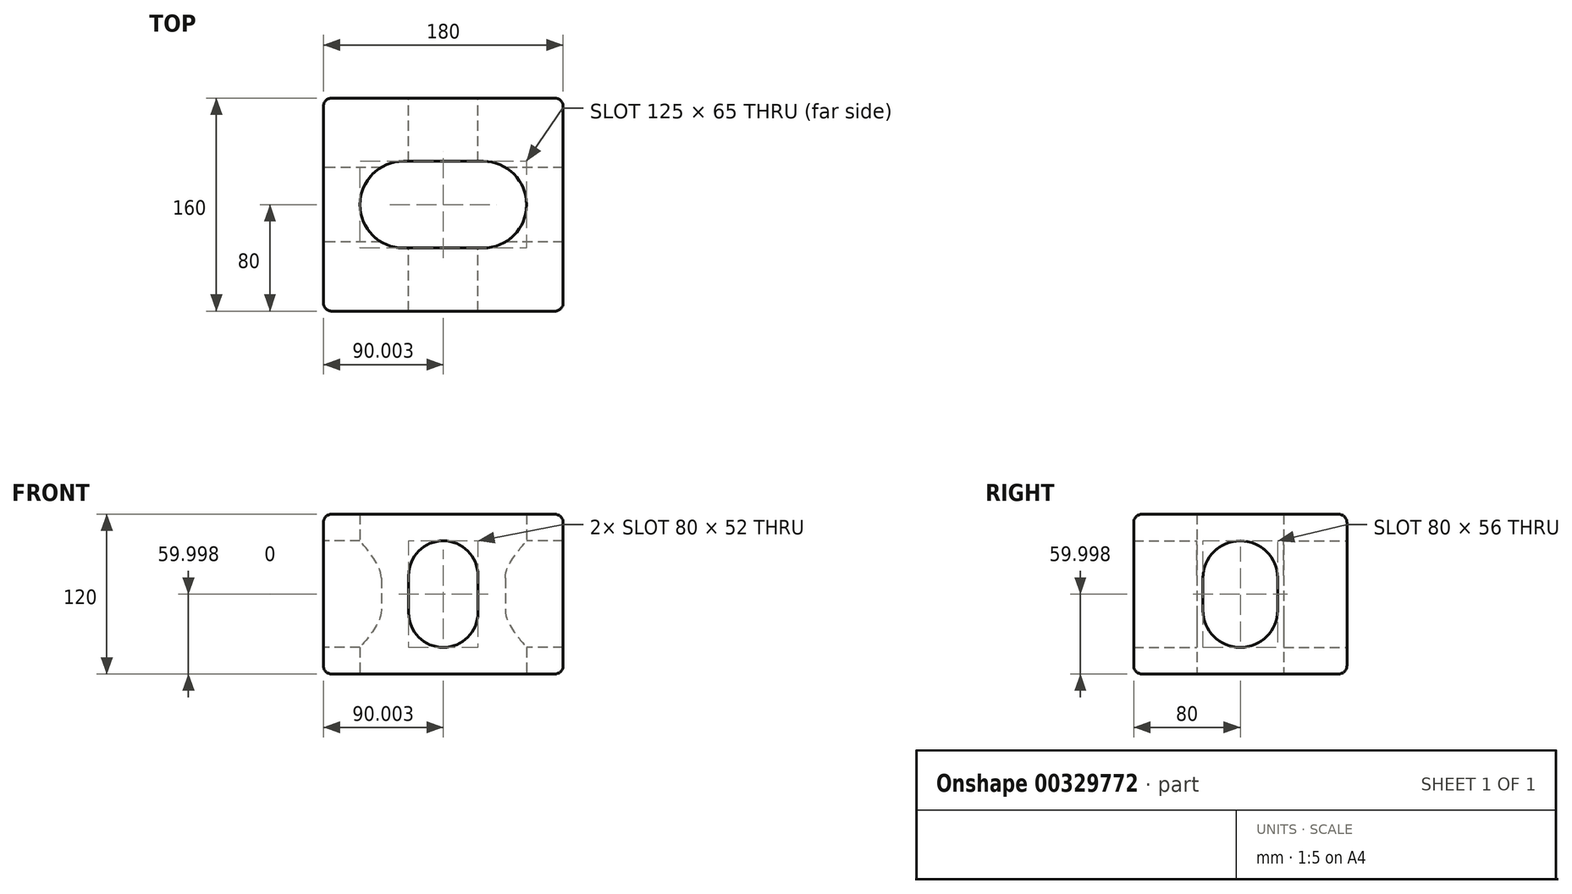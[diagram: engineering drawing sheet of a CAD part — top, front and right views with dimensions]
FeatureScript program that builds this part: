
annotation { "Feature Type Name" : "Feature", "Feature Type Description" : "" }
export const myFeature = defineFeature(function(context is Context, id is Id, definition is map)
    precondition{}
    {
        {
            var Q0;
            Q0=qCreatedBy(makeId("Front.planeOp"),FACE);
            var sketch = newSketch(context, id + "F0", { "sketchPlane" : qUnion([Q0])});
            skLineSegment(sketch, "E0.bottom", {"start": v(-26.88, 79.86) * mm, "end": v(140.42, 79.86) * mm});
            skLineSegment(sketch, "E0.top", {"start": v(-26.88, -40.14) * mm, "end": v(140.42, -40.14) * mm});
            skLineSegment(sketch, "E0.left", {"start": v(-33.23, 73.5) * mm, "end": v(-33.23, -33.8) * mm});
            skLineSegment(sketch, "E0.right", {"start": v(146.77, 73.5) * mm, "end": v(146.77, -33.8) * mm});
            skPoint(sketch, "E1.visualSharp", {"position": v(-33.23, 79.86) * mm});
            skArc(sketch, "E1.filletArc", {"start": v(-26.88, 79.86) * mm, "mid": v(-31.37, 78) * mm, "end": v(-33.23, 73.5) * mm});
            skPoint(sketch, "E2.visualSharp", {"position": v(146.77, 79.86) * mm});
            skArc(sketch, "E2.filletArc", {"start": v(146.77, 73.5) * mm, "mid": v(144.91, 78) * mm, "end": v(140.42, 79.86) * mm});
            skPoint(sketch, "E3.visualSharp", {"position": v(146.77, -40.14) * mm});
            skArc(sketch, "E3.filletArc", {"start": v(140.42, -40.14) * mm, "mid": v(144.91, -38.28) * mm, "end": v(146.77, -33.8) * mm});
            skPoint(sketch, "E4.visualSharp", {"position": v(-33.23, -40.14) * mm});
            skArc(sketch, "E4.filletArc", {"start": v(-33.23, -33.8) * mm, "mid": v(-31.37, -38.28) * mm, "end": v(-26.88, -40.14) * mm});
            skLineSegment(sketch, "E5", {"start": v(30.77, 33.86) * mm, "end": v(30.77, 5.86) * mm});
            skArc(sketch, "E6", {"start": v(30.77, 5.86) * mm, "mid": v(56.77, -20.14) * mm, "end": v(82.77, 5.86) * mm});
            skLineSegment(sketch, "E7", {"start": v(82.77, 5.86) * mm, "end": v(82.77, 33.86) * mm});
            skArc(sketch, "E8", {"start": v(82.77, 33.86) * mm, "mid": v(56.77, 59.86) * mm, "end": v(30.77, 33.86) * mm});
            skSolve(sketch);
        }
        {
            var Q0;
            Q0=makeQuery(id+"F0.imprint","IMPRINT",FACE,{"disambiguationData":[TD([[makeQuery(id+"F0.imprint","IMPRINT",EDGE,{"derivedFrom":sQuery(id+"F0.wireOp",EDGE,"E0.bottom")}),-1.0]])]});
            extrude(context, id + "F1", {"entities" : qUnion([Q0]), "depth" : 160 * mm});
        }
        {
            var Q0;
            Q0=makeQuery(id+"F1.opExtrude","SWEPT_FACE",FACE,{"disambiguationData":[OSD([sQuery(id+"F0.wireOp",EDGE,"E0.top")])]});
            var sketch = newSketch(context, id + "F2", { "sketchPlane" : qUnion([Q0])});
            skLineSegment(sketch, "E9", {"start": v(86.77, 47.5) * mm, "end": v(26.77, 47.5) * mm});
            skArc(sketch, "E10", {"start": v(86.77, 47.5) * mm, "mid": v(119.27, 80) * mm, "end": v(86.77, 112.5) * mm});
            skLineSegment(sketch, "E11", {"start": v(86.77, 112.5) * mm, "end": v(26.77, 112.5) * mm});
            skArc(sketch, "E12", {"start": v(26.77, 112.5) * mm, "mid": v(-5.73, 80) * mm, "end": v(26.77, 47.5) * mm});
            skSolve(sketch);
        }
        {
            var Q0;
            Q0 = qSketchRegion(id + "F2", true);
            extrude(context, id + "F3", {"entities" : qUnion([Q0]), "operationType" : NewBodyOperationType.REMOVE, "oppositeDirection" : true, "depth" : 120 * mm});
        }
        {
            var Q0;
            Q0=makeQuery(id+"F1.opExtrude","SWEPT_FACE",FACE,{"disambiguationData":[OSD([sQuery(id+"F0.wireOp",EDGE,"E0.left")])]});
            var sketch = newSketch(context, id + "F4", { "sketchPlane" : qUnion([Q0])});
            skLineSegment(sketch, "E13", {"start": v(52, 31.86) * mm, "end": v(52, 7.86) * mm});
            skArc(sketch, "E14", {"start": v(52, 7.86) * mm, "mid": v(80, -20.14) * mm, "end": v(108, 7.86) * mm});
            skLineSegment(sketch, "E15", {"start": v(108, 7.86) * mm, "end": v(108, 31.86) * mm});
            skArc(sketch, "E16", {"start": v(108, 31.86) * mm, "mid": v(80, 59.86) * mm, "end": v(52, 31.86) * mm});
            skSolve(sketch);
        }
        {
            var Q0;
            Q0=makeQuery(id+"F4.imprint","IMPRINT",FACE,{"disambiguationData":[TD([[makeQuery(id+"F4.imprint","IMPRINT",EDGE,{"derivedFrom":sQuery(id+"F4.wireOp",EDGE,"E13")}),1.0]])]});
            extrude(context, id + "F5", {"entities" : qUnion([Q0]), "operationType" : NewBodyOperationType.REMOVE, "oppositeDirection" : true, "depth" : 180 * mm});
        }
        {
            var Q0;
            Q0=makeQuery(id+"F1.opExtrude","CAP_EDGE",EDGE,{"disambiguationData":[OSD([sQuery(id+"F0.wireOp",EDGE,"E0.top")])],"isStart":true});
            var Q1;
            Q1=makeQuery(id+"F1.opExtrude","SWEPT_EDGE",EDGE,{"disambiguationData":[OSD([sQuery(id+"F0.wireOp",EDGE,"E0.top"),sQuery(id+"F0.wireOp",EDGE,"E3.filletArc")])]});
            fillet(context, id + "F6", {"entities" : qUnion([Q0, Q1]), "radius" : 6.35 * mm, "tangentPropagation" : true, "allowEdgeOverflow" : false});
        }
        {
            var Q0;
            Q0=makeQuery(id+"F1.opExtrude","CAP_EDGE",EDGE,{"disambiguationData":[OSD([sQuery(id+"F0.wireOp",EDGE,"E0.top")])],"isStart":false});
            var Q1;
            Q1=makeQuery(id+"F1.opExtrude","SWEPT_EDGE",EDGE,{"disambiguationData":[OSD([sQuery(id+"F0.wireOp",EDGE,"E0.top"),sQuery(id+"F0.wireOp",EDGE,"E4.filletArc")])]});
            fillet(context, id + "F7", {"entities" : qUnion([Q0, Q1]), "radius" : 6.35 * mm, "tangentPropagation" : true, "allowEdgeOverflow" : false});
        }
    });
